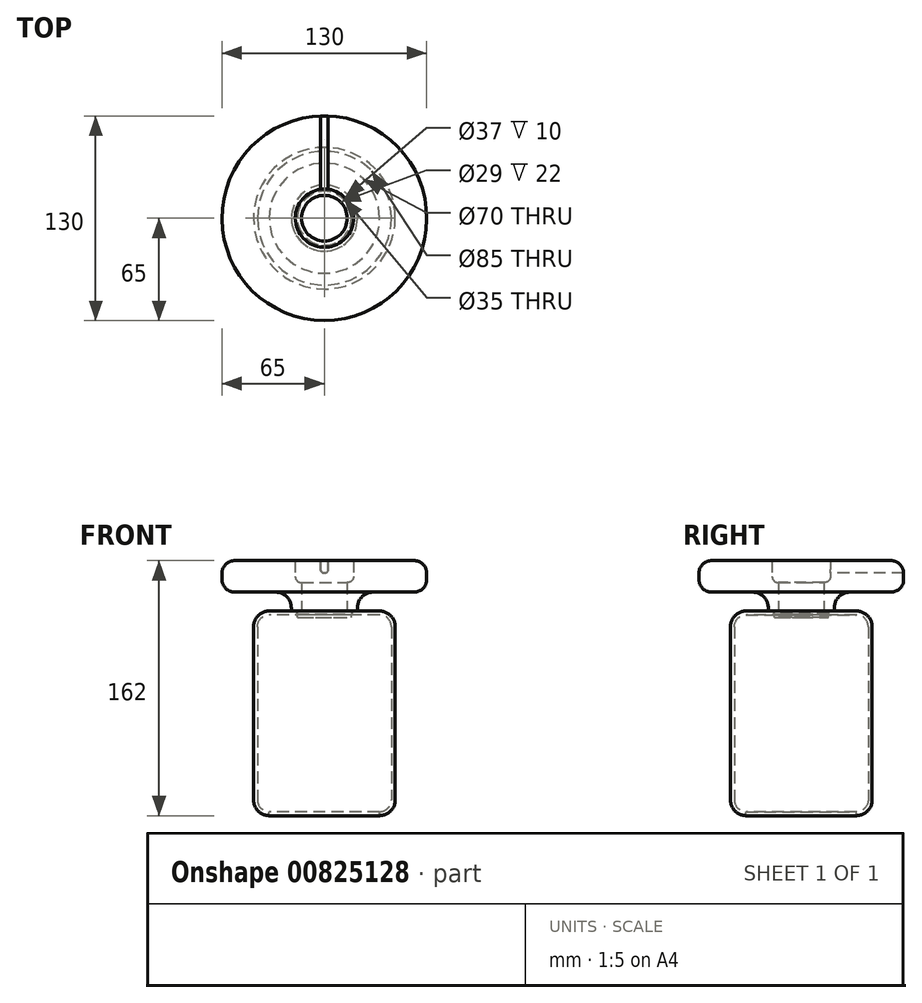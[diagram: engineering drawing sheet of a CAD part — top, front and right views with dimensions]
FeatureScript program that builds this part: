
annotation { "Feature Type Name" : "Feature", "Feature Type Description" : "" }
export const myFeature = defineFeature(function(context is Context, id is Id, definition is map)
    precondition{}
    {
        {
            var Q0;
            Q0=qCreatedBy(makeId("Top.planeOp"),FACE);
            var sketch = newSketch(context, id + "F0", { "sketchPlane" : qUnion([Q0])});
            skCircle(sketch, "E0", {"center": v(0, 0) * mm, "radius": 45 * mm});
            skSolve(sketch);
        }
        {
            var Q0;
            Q0=makeQuery(id+"F0.imprint","IMPRINT",FACE,{"disambiguationData":[TD([[makeQuery(id+"F0.imprint","IMPRINT",EDGE,{"derivedFrom":sQuery(id+"F0.wireOp",EDGE,"E0")}),1.0]])]});
            extrude(context, id + "F1", {"entities" : qUnion([Q0]), "depth" : 130 * mm, "offsetDistance" : 25 * mm});
        }
        {
            var Q0;
            Q0=makeQuery(id+"F1.opExtrude","CAP_EDGE",EDGE,{"disambiguationData":[OSD([sQuery(id+"F0.wireOp",EDGE,"E0")])],"isStart":true});
            var Q1;
            Q1=makeQuery(id+"F1.opExtrude","CAP_EDGE",EDGE,{"disambiguationData":[OSD([sQuery(id+"F0.wireOp",EDGE,"E0")])],"isStart":false});
            fillet(context, id + "F2", {"entities" : qUnion([Q0, Q1]), "tangentPropagation" : true, "radius" : 10 * mm, "defaultsChanged" : true, "vertexSettings" : [], "allowEdgeOverflow" : false});
        }
        {
            var Q0;
            Q0=makeQuery(id+"F1.opExtrude","CAP_FACE",FACE,{"disambiguationData":[OSD([sQuery(id+"F0.wireOp",EDGE,"E0")])],"isStart":true});
            shell(context, id + "F3", {"entities" : qUnion([Q0]), "thickness" : 2.5 * mm});
        }
        {
            var Q0;
            Q0=makeQuery(id+"F1.opExtrude","CAP_FACE",FACE,{"disambiguationData":[OSD([sQuery(id+"F0.wireOp",EDGE,"E0")])],"isStart":false});
            var sketch = newSketch(context, id + "F4", { "sketchPlane" : qUnion([Q0])});
            skCircle(sketch, "E1", {"center": v(0, 0) * mm, "radius": 17.5 * mm});
            skSolve(sketch);
        }
        {
            var Q0;
            Q0 = qSketchRegion(id + "F4", true);
            extrude(context, id + "F5", {"entities" : qUnion([Q0]), "operationType" : NewBodyOperationType.REMOVE, "oppositeDirection" : true, "depth" : 25 * mm, "offsetDistance" : 25 * mm});
        }
        {
            var Q0;
            Q0=makeQuery(id+"F1.opExtrude","CAP_FACE",FACE,{"disambiguationData":[OSD([sQuery(id+"F0.wireOp",EDGE,"E0")])],"isStart":false});
            cPlane(context, id + "F6", {"entities" : qUnion([Q0]), "cplaneType" : CPlaneType.OFFSET, "offset" : 0 * mm, "width" : 150 * mm, "height" : 150 * mm});
        }
        {
            var Q0;
            Q0=qCreatedBy(makeId("Front.planeOp"),FACE);
            var sketch = newSketch(context, id + "F7", { "sketchPlane" : qUnion([Q0])});
            skLineSegment(sketch, "E2", {"start": v(0, 43.5) * mm, "end": v(0, 212.26) * mm, "construction": true});
            skLineSegment(sketch, "E3", {"start": v(65, 142) * mm, "end": v(65, 162) * mm});
            skLineSegment(sketch, "E4", {"start": v(14.5, 148) * mm, "end": v(18.5, 148) * mm});
            skLineSegment(sketch, "E5", {"start": v(18.5, 148) * mm, "end": v(18.5, 162) * mm});
            skLineSegment(sketch, "E6", {"start": v(21, 142) * mm, "end": v(21, 130) * mm});
            skLineSegment(sketch, "E7", {"start": v(65, 142) * mm, "end": v(21, 142) * mm});
            skLineSegment(sketch, "E8", {"start": v(14.5, 126) * mm, "end": v(17.4, 126) * mm});
            skLineSegment(sketch, "E9", {"start": v(17.4, 126) * mm, "end": v(17.4, 130) * mm});
            skLineSegment(sketch, "E10", {"start": v(17.4, 130) * mm, "end": v(21, 130) * mm});
            skLineSegment(sketch, "E11", {"start": v(14.5, 126) * mm, "end": v(14.5, 148) * mm});
            skLineSegment(sketch, "E12", {"start": v(65, 162) * mm, "end": v(18.5, 162) * mm});
            skSolve(sketch);
        }
        {
            var Q0;
            {var subQ3=sQuery(id+"F7.wireOp",EDGE,"2TwXv793-Xn5B-6Ni7-9322-5aZMgMwoWeCw");Q0=makeQuery(id+"F7.imprint","IMPRINT",FACE,{"disambiguationData":[TD([[makeQuery(id+"F7.imprint","IMPRINT",EDGE,{"derivedFrom":subQ3}),1.0]])]});}
            var Q1;
            {var subQ0=sQuery(id+"F7.wireOp",EDGE,"E6");Q1=makeQuery(id+"F7.imprint","IMPRINT",FACE,{"disambiguationData":[TD([[makeQuery(id+"F7.imprint","IMPRINT",EDGE,{"derivedFrom":subQ0}),-1.0]])]});}
            var Q2;
            Q2=sQuery(id+"F7.wireOp",EDGE,"E2");
            revolve(context, id + "F8", {"surfaceOperationType" : NewSurfaceOperationType.NEW, "entities" : qUnion([Q0, Q1]), "axis" : qUnion([Q2]), "revolveType" : RevolveType.FULL});
        }
        {
            var Q0;
            Q0=makeQuery(id+"F8.opRevolve","SWEPT_EDGE",EDGE,{"disambiguationData":[OSD([sQuery(id+"F7.wireOp",EDGE,"2TwXv793-Xn5B-6Ni7-9322-5aZMgMwoWeCw"),sQuery(id+"F7.wireOp",EDGE,"E3")])]});
            fillet(context, id + "F9", {"entities" : qUnion([Q0]), "tangentPropagation" : true, "radius" : 8 * mm, "defaultsChanged" : true, "vertexSettings" : [], "allowEdgeOverflow" : false});
        }
        {
            var Q0;
            Q0=makeQuery(id+"F8.opRevolve","SWEPT_EDGE",EDGE,{"disambiguationData":[OSD([sQuery(id+"F7.wireOp",EDGE,"E6"),sQuery(id+"F7.wireOp",EDGE,"E7")])]});
            fillet(context, id + "F10", {"entities" : qUnion([Q0]), "tangentPropagation" : true, "radius" : 10 * mm, "defaultsChanged" : true, "vertexSettings" : [], "allowEdgeOverflow" : false});
        }
        {
            var Q0;
            Q0=makeQuery(id+"F8.opRevolve","SWEPT_EDGE",EDGE,{"disambiguationData":[OSD([sQuery(id+"F7.wireOp",EDGE,"E8"),sQuery(id+"F7.wireOp",EDGE,"E9")])]});
            chamfer(context, id + "F11", {"entities" : qUnion([Q0]), "chamferType" : ChamferType.TWO_OFFSETS, "width1" : 0.3 * mm, "oppositeDirection" : false, "width2" : 2 * mm, "tangentPropagation" : true});
        }
        {
            var Q0;
            Q0=qCreatedBy(makeId("Front.planeOp"),FACE);
            var sketch = newSketch(context, id + "F12", { "sketchPlane" : qUnion([Q0])});
            skLineSegment(sketch, "E13.bottom", {"start": v(-2.35, 162) * mm, "end": v(2.35, 162) * mm});
            skLineSegment(sketch, "E13.top", {"start": v(-2.35, 154) * mm, "end": v(2.35, 154) * mm});
            skLineSegment(sketch, "E13.left", {"start": v(-2.35, 162) * mm, "end": v(-2.35, 154) * mm});
            skLineSegment(sketch, "E13.right", {"start": v(2.35, 162) * mm, "end": v(2.35, 154) * mm});
            skSolve(sketch);
        }
        {
            var Q0;
            Q0 = qSketchRegion(id + "F12", true);
            extrude(context, id + "F13", {"entities" : qUnion([Q0]), "operationType" : NewBodyOperationType.REMOVE, "oppositeDirection" : true, "depth" : 100 * mm, "offsetDistance" : 25 * mm});
        }
        {
            var Q0;
            Q0=makeQuery(id+"F13.boolean.opBoolean","COPY",EDGE,{"derivedFrom":makeQuery(id+"F13.opExtrude","SWEPT_EDGE",EDGE,{"disambiguationData":[OSD([sQuery(id+"F12.wireOp",EDGE,"E13.top"),sQuery(id+"F12.wireOp",EDGE,"E13.left")])]})});
            var Q1;
            Q1=makeQuery(id+"F13.boolean.opBoolean","COPY",EDGE,{"derivedFrom":makeQuery(id+"F13.opExtrude","SWEPT_EDGE",EDGE,{"disambiguationData":[OSD([sQuery(id+"F12.wireOp",EDGE,"E13.top"),sQuery(id+"F12.wireOp",EDGE,"E13.right")])]})});
            fillet(context, id + "F14", {"entities" : qUnion([Q0, Q1]), "tangentPropagation" : true, "radius" : 2.3 * mm, "defaultsChanged" : true, "vertexSettings" : [], "allowEdgeOverflow" : false});
        }
        {
            var Q0;
            Q0=makeQuery(id+"F8.opRevolve","SWEPT_EDGE",EDGE,{"disambiguationData":[OSD([sQuery(id+"F7.wireOp",EDGE,"E4"),sQuery(id+"F7.wireOp",EDGE,"E5")])]});
            fillet(context, id + "F15", {"entities" : qUnion([Q0]), "tangentPropagation" : true, "radius" : 4 * mm, "defaultsChanged" : true, "vertexSettings" : [], "allowEdgeOverflow" : false});
        }
    });
